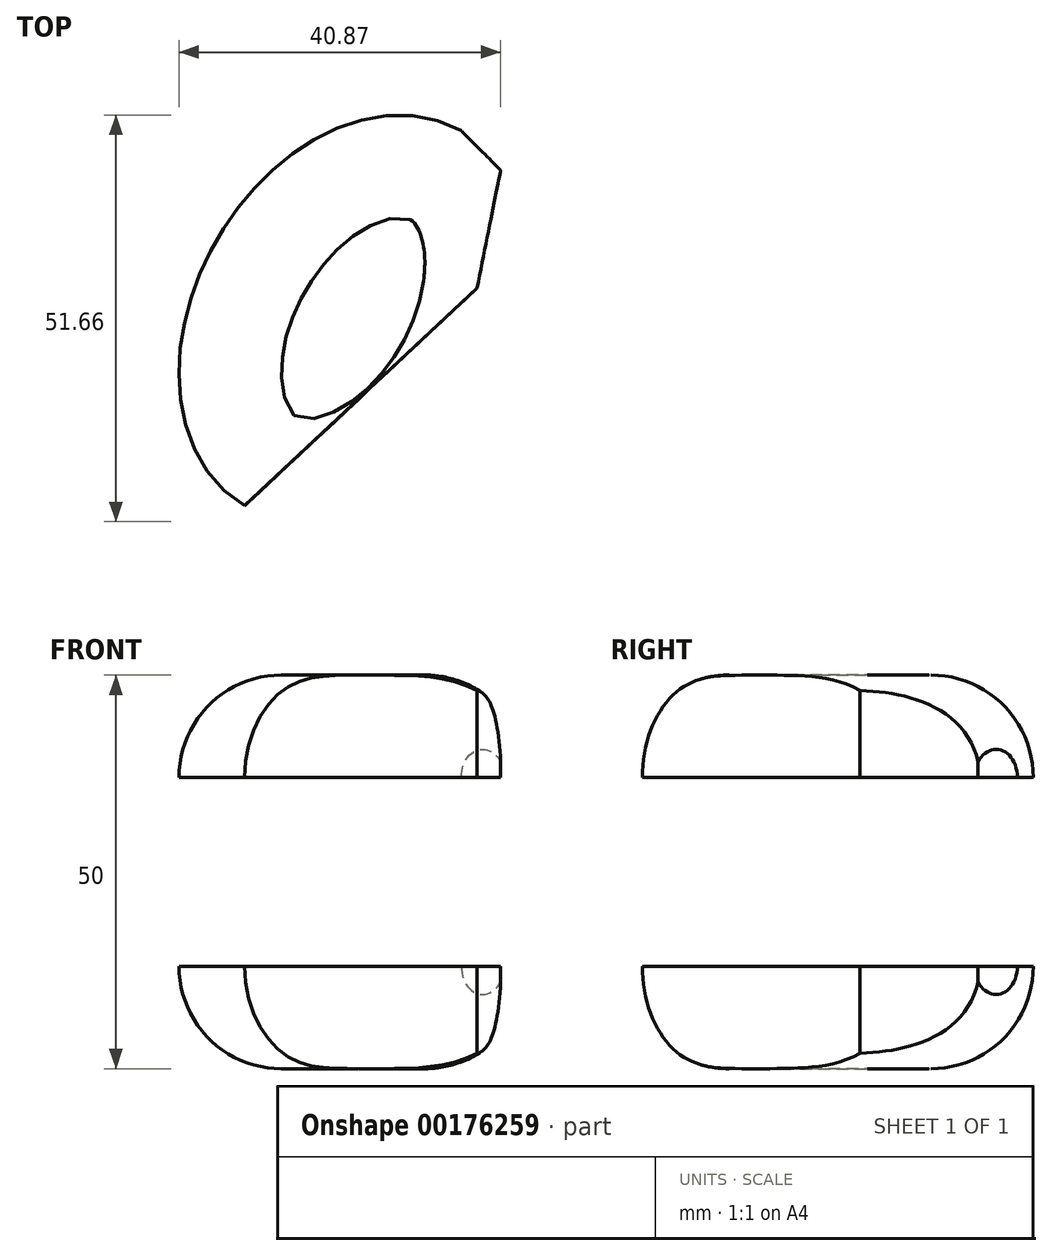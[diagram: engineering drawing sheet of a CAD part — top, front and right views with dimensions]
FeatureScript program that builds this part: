
annotation { "Feature Type Name" : "Feature", "Feature Type Description" : "" }
export const myFeature = defineFeature(function(context is Context, id is Id, definition is map)
    precondition{}
    {
        {
            var Q0;
            Q0=qCreatedBy(makeId("Top.planeOp"),FACE);
            var sketch = newSketch(context, id + "F0", { "sketchPlane" : qUnion([Q0])});
            skEllipticalArc(sketch, "E0", {});
            skPoint(sketch, "E1", {"position": v(13.75, 23.82) * mm});
            skPoint(sketch, "E2", {"position": v(-17.32, 10) * mm});
            skLineSegment(sketch, "E3", {"start": v(13.75, 23.82) * mm, "end": v(0, 0) * mm, "construction": true});
            skLineSegment(sketch, "E4", {"start": v(0, 0) * mm, "end": v(-13.75, -23.82) * mm, "construction": true});
            skLineSegment(sketch, "E5", {"start": v(13.75, 23.82) * mm, "end": v(18.75, 18.82) * mm});
            skLineSegment(sketch, "E6", {"start": v(18.75, 18.82) * mm, "end": v(15.75, 3.82) * mm});
            skLineSegment(sketch, "E7", {"start": v(15.75, 3.82) * mm, "end": v(-13.75, -23.82) * mm});
            const initialGuessF0  = {"E0": [0, 0, 0.5, 0.8660254037844386, 0.0275, 0.02, 0, 3.141592653589793]};
            skSetInitialGuess(sketch, initialGuessF0);
            skSolve(sketch);
        }
        {
            var Q0;
            Q0=qSketchRegion(id+"F0",true);
            extrude(context, id + "F1", {"entities" : qUnion([Q0]), "depth" : 25 * mm, "hasSecondDirection" : true, "secondDirectionOppositeDirection" : true, "secondDirectionDepth" : 25 * mm});
        }
        {
            var Q0;
            Q0=makeQuery(id+"F1.opExtrude","CAP_EDGE",EDGE,{"disambiguationData":[OSD([sQuery(id+"F0.wireOp",EDGE,"E0")])],"isStart":true});
            var Q1;
            Q1=makeQuery(id+"F1.opExtrude","CAP_EDGE",EDGE,{"disambiguationData":[OSD([sQuery(id+"F0.wireOp",EDGE,"E0")])],"isStart":false});
            fillet(context, id + "F2", {"entities" : qUnion([Q0, Q1]), "radius" : 13 * mm, "tangentPropagation" : true, "allowEdgeOverflow" : false});
        }
        {
            var Q0;
            Q0=qCreatedBy(makeId("Front.planeOp"),FACE);
            var sketch = newSketch(context, id + "F3", { "sketchPlane" : qUnion([Q0])});
            skLineSegment(sketch, "E8.0", {"start": v(18.75, 14.02) * mm, "end": v(18.75, -14.02) * mm, "construction": true});
            skFitSpline(sketch, "E9.0", {"points": [v(-9.11, -25) * mm, v(-3.04, -25) * mm, v(3.04, -25) * mm, v(9.11, -25) * mm], "construction": true});
            skLineSegment(sketch, "E10", {"start": v(-22.11, -12) * mm, "end": v(-22.11, 12) * mm, "construction": true});
            skLineSegment(sketch, "E11.bottom", {"start": v(18.75, 0) * mm, "end": v(-22.11, 0) * mm});
            skLineSegment(sketch, "E11.top", {"start": v(18.75, -25) * mm, "end": v(-22.11, -25) * mm});
            skLineSegment(sketch, "E11.left", {"start": v(18.75, 0) * mm, "end": v(18.75, -25) * mm});
            skLineSegment(sketch, "E11.right", {"start": v(-22.11, 0) * mm, "end": v(-22.11, -25) * mm});
            skLineSegment(sketch, "E12.bottom", {"start": v(-22.11, 0) * mm, "end": v(18.75, 0) * mm});
            skLineSegment(sketch, "E12.top", {"start": v(-22.11, 12) * mm, "end": v(18.75, 12) * mm});
            skLineSegment(sketch, "E12.left", {"start": v(-22.11, 0) * mm, "end": v(-22.11, 12) * mm});
            skLineSegment(sketch, "E12.right", {"start": v(18.75, 0) * mm, "end": v(18.75, 12) * mm});
            skSolve(sketch);
        }
        {
            var Q0;
            Q0=qSketchRegion(id+"F3",true);
            extrude(context, id + "F4", {"entities" : qUnion([Q0]), "operationType" : NewBodyOperationType.REMOVE, "endBound" : BoundingType.THROUGH_ALL, "oppositeDirection" : true, "depth" : 25 * mm, "hasSecondDirection" : true, "secondDirectionBound" : SecondDirectionBoundingType.THROUGH_ALL, "secondDirectionOppositeDirection" : false, "secondDirectionDepth" : 25 * mm});
        }
        {
            var Q0;
            Q0=makeQuery(id+"F1.opExtrude","SWEPT_BODY",BODY,{"disambiguationData":[OSD([sQuery(id+"F0.wireOp",EDGE,"E0"),sQuery(id+"F0.wireOp",EDGE,"E5"),sQuery(id+"F0.wireOp",EDGE,"E6"),sQuery(id+"F0.wireOp",EDGE,"E7")])]});
            var Q1;
            Q1=qCreatedBy(makeId("Top.planeOp"),FACE);
            mirror(context, id + "F5", {"entities" : qUnion([Q0]), "mirrorPlane" : qUnion([Q1])});
        }
    });
